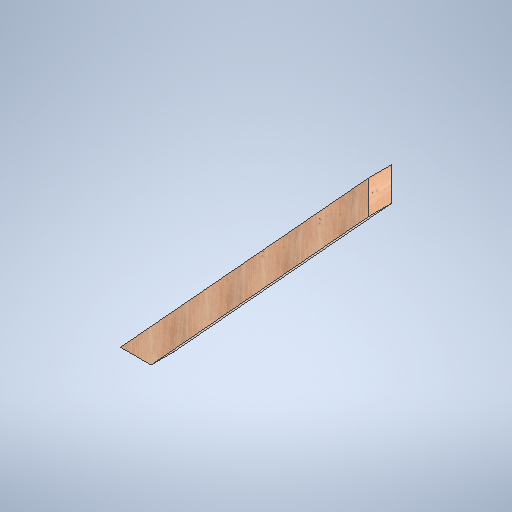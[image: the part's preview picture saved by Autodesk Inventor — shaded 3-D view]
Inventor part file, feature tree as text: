
AUTODESK INVENTOR PART (.ipt)
format: ipt  version: 2025 (Build 290162000, 162)  size: 280,064 bytes
history: native  units: in
note: dims shown in document units (in); Inventor stores cm internally (conversion verified against a paired STEP export)
features: extrude x1, sketch x1
ambient origin geometry x8: Origin, YZ Plane, XZ Plane, XY Plane, X Axis, Y Axis, Z Axis, Center Point
bodies: Solid1 (feature_tree)
feature tree (2):
  extrude  "Extrusion1"  Depth=4.0in TaperAngle=0.0deg
  sketch  "Sketch1"  dims[d0=4.0in d1=4.0in d2=0.0in]
